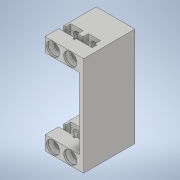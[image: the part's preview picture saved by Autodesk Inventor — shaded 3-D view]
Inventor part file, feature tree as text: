
AUTODESK INVENTOR PART (.ipt)
format: ipt  version: 2020 (Build 240168000, 168)  size: 198,656 bytes
history: native  units: mm
features: other x3, extrude x2, sketch x2, pattern_linear x1
ambient origin geometry x8: Origin, YZ Plane, XZ Plane, XY Plane, X Axis, Y Axis, Z Axis, Center Point
bodies: Solide1 (feature_tree)
feature tree (8):
  other  "base2.ipt"
  pattern_linear  "Réseau rectangulaire1"  Spacing1=10.0mm  [1 undecoded]
  extrude  "Extrusion1"  Depth=20.0mm
  extrude  "Extrusion2"  Depth=49.78mm
  other  "Solide1::base2.ipt"
  other  "FonctionRepérage1"
  sketch  "Esquisse2"
  sketch  "Esquisse3"
note: 1 required parameter value undecoded (feature->parameter linkage not recoverable at this tier; creation-order binding heuristic only, values carry confidence <= 0.55)
